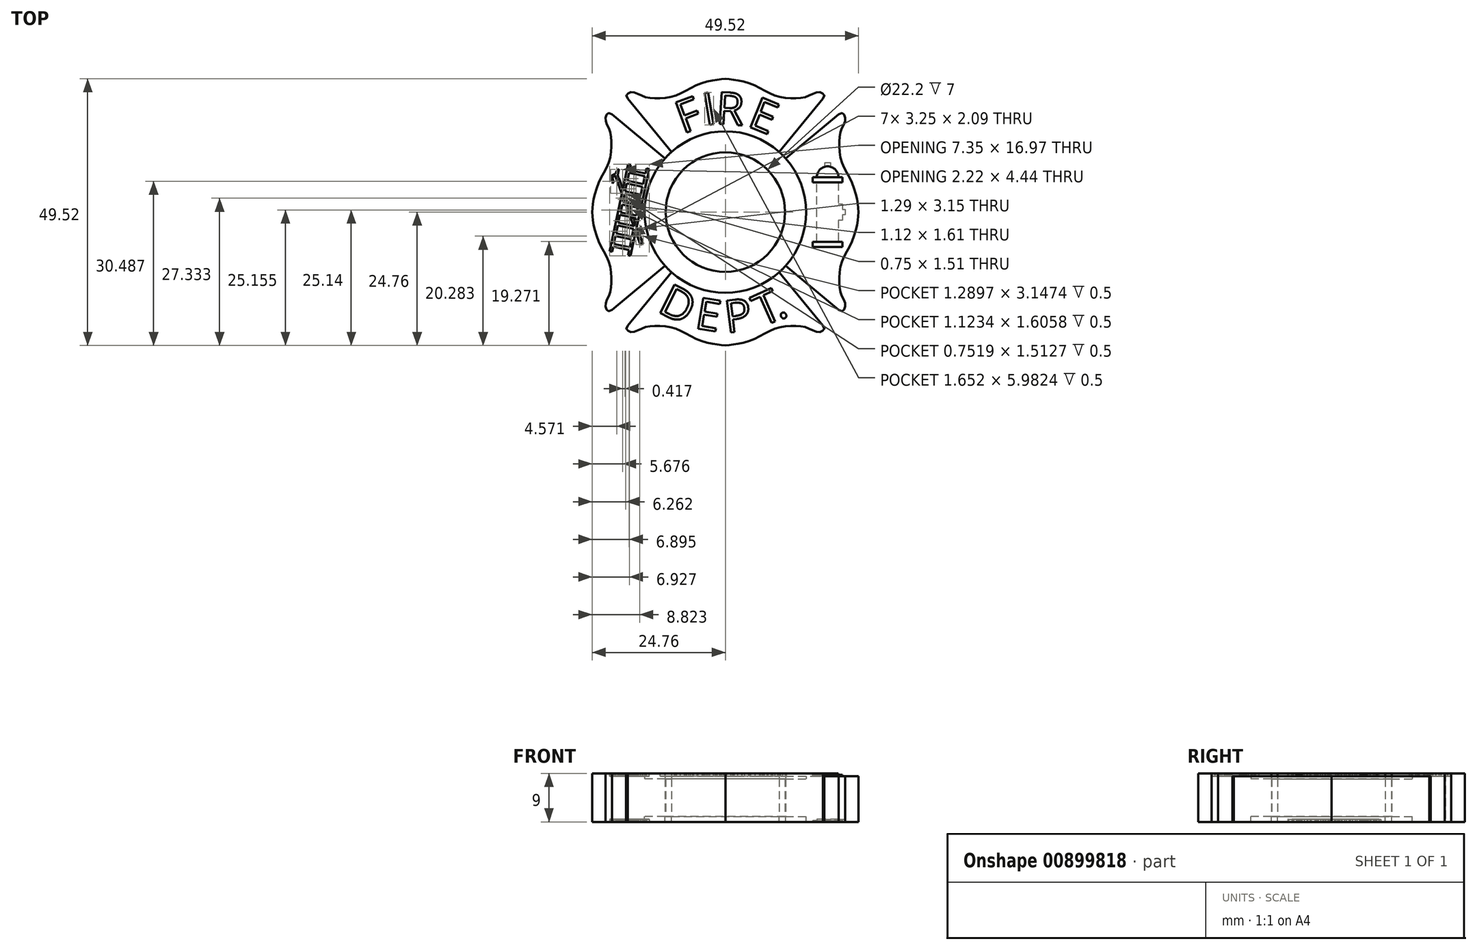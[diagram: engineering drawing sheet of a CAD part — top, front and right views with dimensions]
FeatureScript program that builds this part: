
annotation { "Feature Type Name" : "Feature", "Feature Type Description" : "" }
export const myFeature = defineFeature(function(context is Context, id is Id, definition is map)
    precondition{}
    {
        {
            var Q0;
            Q0=qCreatedBy(makeId("Top.planeOp"),FACE);
            var sketch = newSketch(context, id + "F0", { "sketchPlane" : qUnion([Q0])});
            skCircle(sketch, "E0", {"center": v(0, 0) * mm, "radius": 11.1 * mm});
            skCircle(sketch, "E1", {"center": v(0, 0) * mm, "radius": 15 * mm});
            skLineSegment(sketch, "E2", {"start": v(-30.5, 30.5) * mm, "end": v(0, 0) * mm, "construction": true});
            skLineSegment(sketch, "E3", {"start": v(0, 0) * mm, "end": v(35.07, -35.07) * mm, "construction": true});
            skLineSegment(sketch, "E4", {"start": v(31.52, 31.52) * mm, "end": v(-34.6, -34.6) * mm, "construction": true});
            skLineSegment(sketch, "E5", {"start": v(-10, 11.18) * mm, "end": v(-18.15, 21.05) * mm});
            skFitSpline(sketch, "E6", {"points": [v(-18.15, 21.05) * mm, v(-18.15, 22) * mm, v(-17.03, 22.25) * mm, v(-15.24, 21.5) * mm, v(-12.76, 21.15) * mm, v(-9.23, 21.64) * mm, v(-5.9, 23.34) * mm, v(-2.2, 24.5) * mm, v(0, 24.76) * mm], "startDerivative": vector(-16.22, 16.71) * mm, "endDerivative": vector(16.44, 1.31) * mm});
            skLineSegment(sketch, "E7", {"start": v(0, 15) * mm, "end": v(0, 24.76) * mm, "construction": true});
            skFitSpline(sketch, "E8.MirrorCS", {"points": [v(18.15, 21.05) * mm, v(18.15, 22) * mm, v(17.03, 22.25) * mm, v(15.24, 21.5) * mm, v(12.76, 21.15) * mm, v(9.23, 21.64) * mm, v(5.9, 23.34) * mm, v(2.2, 24.5) * mm, v(0, 24.76) * mm], "startDerivative": vector(16.22, 16.71) * mm, "endDerivative": vector(-16.44, 1.31) * mm});
            skLineSegment(sketch, "E9.MirrorCS", {"start": v(10, 11.18) * mm, "end": v(18.15, 21.05) * mm});
            skLineSegment(sketch, "E10", {"start": v(11.18, 10) * mm, "end": v(21.05, 18.15) * mm});
            skFitSpline(sketch, "E11", {"points": [v(21.05, 18.15) * mm, v(22, 18.15) * mm, v(22.25, 17.03) * mm, v(21.5, 15.24) * mm, v(21.15, 12.76) * mm, v(21.64, 9.23) * mm, v(23.34, 5.9) * mm, v(24.5, 2.2) * mm, v(24.76, 0) * mm], "startDerivative": vector(16.71, 16.22) * mm, "endDerivative": vector(1.31, -16.44) * mm});
            skLineSegment(sketch, "E12", {"start": v(15, 0) * mm, "end": v(24.76, 0) * mm, "construction": true});
            skFitSpline(sketch, "E13.MirrorCS", {"points": [v(21.05, -18.15) * mm, v(22, -18.15) * mm, v(22.25, -17.03) * mm, v(21.5, -15.24) * mm, v(21.15, -12.76) * mm, v(21.64, -9.23) * mm, v(23.34, -5.9) * mm, v(24.5, -2.2) * mm, v(24.76, 0) * mm], "startDerivative": vector(16.71, -16.22) * mm, "endDerivative": vector(1.31, 16.44) * mm});
            skLineSegment(sketch, "E14.MirrorCS", {"start": v(11.18, -10) * mm, "end": v(21.05, -18.15) * mm});
            skPoint(sketch, "E15", {"position": v(15, 0) * mm});
            skLineSegment(sketch, "E16", {"start": v(10, -11.18) * mm, "end": v(18.15, -21.05) * mm});
            skFitSpline(sketch, "E17", {"points": [v(18.15, -21.05) * mm, v(18.15, -22) * mm, v(17.03, -22.25) * mm, v(15.24, -21.5) * mm, v(12.76, -21.15) * mm, v(9.23, -21.64) * mm, v(5.9, -23.34) * mm, v(2.2, -24.5) * mm, v(0, -24.76) * mm], "startDerivative": vector(16.22, -16.71) * mm, "endDerivative": vector(-16.44, -1.31) * mm});
            skLineSegment(sketch, "E18", {"start": v(0, -15) * mm, "end": v(0, -24.76) * mm, "construction": true});
            skFitSpline(sketch, "E19.MirrorCS", {"points": [v(-18.15, -21.05) * mm, v(-18.15, -22) * mm, v(-17.03, -22.25) * mm, v(-15.24, -21.5) * mm, v(-12.76, -21.15) * mm, v(-9.23, -21.64) * mm, v(-5.9, -23.34) * mm, v(-2.2, -24.5) * mm, v(0, -24.76) * mm], "startDerivative": vector(-16.22, -16.71) * mm, "endDerivative": vector(16.44, -1.31) * mm});
            skLineSegment(sketch, "E20.MirrorCS", {"start": v(-10, -11.18) * mm, "end": v(-18.15, -21.05) * mm});
            skPoint(sketch, "E21", {"position": v(0, -15) * mm});
            skLineSegment(sketch, "E22", {"start": v(-11.18, -10) * mm, "end": v(-21.05, -18.15) * mm});
            skFitSpline(sketch, "E23", {"points": [v(-21.05, -18.15) * mm, v(-22, -18.15) * mm, v(-22.25, -17.03) * mm, v(-21.5, -15.24) * mm, v(-21.15, -12.76) * mm, v(-21.64, -9.23) * mm, v(-23.34, -5.9) * mm, v(-24.5, -2.2) * mm, v(-24.76, 0) * mm], "startDerivative": vector(-16.71, -16.22) * mm, "endDerivative": vector(-1.31, 16.44) * mm});
            skLineSegment(sketch, "E24", {"start": v(-15, 0) * mm, "end": v(-24.76, 0) * mm, "construction": true});
            skFitSpline(sketch, "E25.MirrorCS", {"points": [v(-21.05, 18.15) * mm, v(-22, 18.15) * mm, v(-22.25, 17.03) * mm, v(-21.5, 15.24) * mm, v(-21.15, 12.76) * mm, v(-21.64, 9.23) * mm, v(-23.34, 5.9) * mm, v(-24.5, 2.2) * mm, v(-24.76, 0) * mm], "startDerivative": vector(-16.71, 16.22) * mm, "endDerivative": vector(-1.31, -16.44) * mm});
            skLineSegment(sketch, "E26.MirrorCS", {"start": v(-11.18, 10) * mm, "end": v(-21.05, 18.15) * mm});
            skPoint(sketch, "E27", {"position": v(-15, 0) * mm});
            skSolve(sketch);
        }
        {
            var Q0;
            {var subQ0=sQuery(id+"F0.wireOp",EDGE,"E22");Q0=makeQuery(id+"F0.imprint","IMPRINT",FACE,{"disambiguationData":[TD([[makeQuery(id+"F0.imprint","IMPRINT",EDGE,{"derivedFrom":subQ0}),-1.0]])]});}
            var Q1;
            {var subQ0=sQuery(id+"F0.wireOp",EDGE,"E5");Q1=makeQuery(id+"F0.imprint","IMPRINT",FACE,{"disambiguationData":[TD([[makeQuery(id+"F0.imprint","IMPRINT",EDGE,{"derivedFrom":subQ0}),-1.0]])]});}
            var Q2;
            {var subQ0=sQuery(id+"F0.wireOp",EDGE,"E10");Q2=makeQuery(id+"F0.imprint","IMPRINT",FACE,{"disambiguationData":[TD([[makeQuery(id+"F0.imprint","IMPRINT",EDGE,{"derivedFrom":subQ0}),-1.0]])]});}
            var Q3;
            {var subQ0=sQuery(id+"F0.wireOp",EDGE,"E16");Q3=makeQuery(id+"F0.imprint","IMPRINT",FACE,{"disambiguationData":[TD([[makeQuery(id+"F0.imprint","IMPRINT",EDGE,{"derivedFrom":subQ0}),-1.0]])]});}
            var Q4;
            Q4=makeQuery(id+"F0.imprint","IMPRINT",FACE,{"disambiguationData":[TD([[makeQuery(id+"F0.imprint","IMPRINT",EDGE,{"derivedFrom":sQuery(id+"F0.wireOp",EDGE,"E0")}),-1.0]])]});
            extrude(context, id + "F1", {"entities" : qUnion([Q0, Q1, Q2, Q3, Q4]), "depth" : 7 * mm, "offsetDistance" : 25 * mm});
        }
        {
            var Q0;
            {var subQ0=sQuery(id+"F0.wireOp",EDGE,"E5");Q0=makeQuery(id+"F0.imprint","IMPRINT",FACE,{"disambiguationData":[TD([[makeQuery(id+"F0.imprint","IMPRINT",EDGE,{"derivedFrom":subQ0}),-1.0]])]});}
            var Q1;
            {var subQ0=sQuery(id+"F0.wireOp",EDGE,"E22");Q1=makeQuery(id+"F0.imprint","IMPRINT",FACE,{"disambiguationData":[TD([[makeQuery(id+"F0.imprint","IMPRINT",EDGE,{"derivedFrom":subQ0}),-1.0]])]});}
            var Q2;
            {var subQ0=sQuery(id+"F0.wireOp",EDGE,"E16");Q2=makeQuery(id+"F0.imprint","IMPRINT",FACE,{"disambiguationData":[TD([[makeQuery(id+"F0.imprint","IMPRINT",EDGE,{"derivedFrom":subQ0}),-1.0]])]});}
            var Q3;
            {var subQ0=sQuery(id+"F0.wireOp",EDGE,"E10");Q3=makeQuery(id+"F0.imprint","IMPRINT",FACE,{"disambiguationData":[TD([[makeQuery(id+"F0.imprint","IMPRINT",EDGE,{"derivedFrom":subQ0}),-1.0]])]});}
            extrude(context, id + "F2", {"entities" : qUnion([Q0, Q1, Q2, Q3]), "operationType" : NewBodyOperationType.ADD, "depth" : 8 * mm, "offsetDistance" : 25 * mm});
        }
        {
            var Q0;
            {var subQ0=sQuery(id+"F0.wireOp",EDGE,"E5");Q0=makeQuery(id+"F0.imprint","IMPRINT",FACE,{"disambiguationData":[TD([[makeQuery(id+"F0.imprint","IMPRINT",EDGE,{"derivedFrom":subQ0}),-1.0]])]});}
            var Q1;
            {var subQ0=sQuery(id+"F0.wireOp",EDGE,"E22");Q1=makeQuery(id+"F0.imprint","IMPRINT",FACE,{"disambiguationData":[TD([[makeQuery(id+"F0.imprint","IMPRINT",EDGE,{"derivedFrom":subQ0}),-1.0]])]});}
            var Q2;
            {var subQ0=sQuery(id+"F0.wireOp",EDGE,"E16");Q2=makeQuery(id+"F0.imprint","IMPRINT",FACE,{"disambiguationData":[TD([[makeQuery(id+"F0.imprint","IMPRINT",EDGE,{"derivedFrom":subQ0}),-1.0]])]});}
            var Q3;
            {var subQ0=sQuery(id+"F0.wireOp",EDGE,"E10");Q3=makeQuery(id+"F0.imprint","IMPRINT",FACE,{"disambiguationData":[TD([[makeQuery(id+"F0.imprint","IMPRINT",EDGE,{"derivedFrom":subQ0}),-1.0]])]});}
            extrude(context, id + "F3", {"entities" : qUnion([Q0, Q1, Q2, Q3]), "operationType" : NewBodyOperationType.ADD, "oppositeDirection" : true, "depth" : 1 * mm, "offsetDistance" : 25 * mm});
        }
        {
            var Q0;
            Q0=makeQuery(id+"F2.opExtrude","CAP_FACE",FACE,{"disambiguationData":[OSD([sQuery(id+"F0.wireOp",EDGE,"E1"),sQuery(id+"F0.wireOp",EDGE,"E22"),sQuery(id+"F0.wireOp",EDGE,"E23"),sQuery(id+"F0.wireOp",EDGE,"E25.MirrorCS"),sQuery(id+"F0.wireOp",EDGE,"E26.MirrorCS")])],"isStart":false});
            var sketch = newSketch(context, id + "F4", { "sketchPlane" : qUnion([Q0])});
            skLineSegment(sketch, "E28", {"start": v(-14.16, 8.03) * mm, "end": v(-17.6, -8.1) * mm});
            skLineSegment(sketch, "E29", {"start": v(-17.6, -8.1) * mm, "end": v(-18.09, -8) * mm});
            skLineSegment(sketch, "E30", {"start": v(-18.09, -8) * mm, "end": v(-14.65, 8.14) * mm});
            skLineSegment(sketch, "E31", {"start": v(-14.65, 8.14) * mm, "end": v(-14.16, 8.03) * mm});
            skLineSegment(sketch, "E32", {"start": v(-14.16, 8.03) * mm, "end": v(-18.88, 9.04) * mm, "construction": true});
            skLineSegment(sketch, "E33", {"start": v(-17.6, -8.1) * mm, "end": v(-22.13, -7.14) * mm, "construction": true});
            skLineSegment(sketch, "E34", {"start": v(-17.58, 8.76) * mm, "end": v(-21.02, -7.38) * mm});
            skLineSegment(sketch, "E35", {"start": v(-21.02, -7.38) * mm, "end": v(-21.5, -7.27) * mm});
            skLineSegment(sketch, "E36", {"start": v(-21.5, -7.27) * mm, "end": v(-18.07, 8.87) * mm});
            skLineSegment(sketch, "E37", {"start": v(-18.07, 8.87) * mm, "end": v(-17.58, 8.76) * mm});
            skLineSegment(sketch, "E38", {"start": v(-17.79, 7.78) * mm, "end": v(-14.85, 7.16) * mm});
            skLineSegment(sketch, "E39", {"start": v(-14.96, 6.67) * mm, "end": v(-17.9, 7.3) * mm});
            skLineSegment(sketch, "E40", {"start": v(-18.2, 5.83) * mm, "end": v(-15.27, 5.2) * mm});
            skLineSegment(sketch, "E41", {"start": v(-15.38, 4.71) * mm, "end": v(-18.3, 5.34) * mm});
            skLineSegment(sketch, "E42", {"start": v(-18.62, 3.87) * mm, "end": v(-15.69, 3.25) * mm});
            skLineSegment(sketch, "E43", {"start": v(-15.8, 2.76) * mm, "end": v(-18.73, 3.38) * mm});
            skLineSegment(sketch, "E44", {"start": v(-19.04, 1.91) * mm, "end": v(-16.1, 1.29) * mm});
            skLineSegment(sketch, "E45", {"start": v(-16.2, 0.8) * mm, "end": v(-19.14, 1.43) * mm});
            skLineSegment(sketch, "E46", {"start": v(-19.46, -0.04) * mm, "end": v(-16.52, -0.67) * mm});
            skLineSegment(sketch, "E47", {"start": v(-16.63, -1.16) * mm, "end": v(-19.56, -0.53) * mm});
            skLineSegment(sketch, "E48", {"start": v(-19.56, -0.53) * mm, "end": v(-19.87, -2) * mm});
            skLineSegment(sketch, "E49", {"start": v(-19.87, -2) * mm, "end": v(-16.94, -2.62) * mm});
            skLineSegment(sketch, "E50", {"start": v(-17.04, -3.11) * mm, "end": v(-19.98, -2.49) * mm});
            skLineSegment(sketch, "E51", {"start": v(-20.3, -3.95) * mm, "end": v(-17.36, -4.58) * mm});
            skLineSegment(sketch, "E52", {"start": v(-17.46, -5.07) * mm, "end": v(-20.4, -4.44) * mm});
            skLineSegment(sketch, "E53", {"start": v(-20.7, -5.9) * mm, "end": v(-17.77, -6.53) * mm});
            skLineSegment(sketch, "E54", {"start": v(-20.81, -6.4) * mm, "end": v(-17.88, -7.02) * mm});
            skLineSegment(sketch, "E55", {"start": v(-15.76, -6.05) * mm, "end": v(-20.25, 6.15) * mm, "construction": true});
            skLineSegment(sketch, "E56", {"start": v(-15.07, -6.49) * mm, "end": v(-19.96, 6.8) * mm, "construction": true});
            skLineSegment(sketch, "E57", {"start": v(-15.76, -6.05) * mm, "end": v(-16.58, -3.82) * mm});
            skLineSegment(sketch, "E58", {"start": v(-16.58, -3.82) * mm, "end": v(-16.39, -2.9) * mm});
            skLineSegment(sketch, "E59", {"start": v(-16.39, -2.9) * mm, "end": v(-15.3, -5.88) * mm});
            skLineSegment(sketch, "E60", {"start": v(-15.3, -5.88) * mm, "end": v(-15.76, -6.05) * mm});
            skLineSegment(sketch, "E61", {"start": v(-17.6, -1.07) * mm, "end": v(-17.02, -1.19) * mm});
            skLineSegment(sketch, "E62", {"start": v(-17.02, -1.19) * mm, "end": v(-16.84, -1.66) * mm});
            skLineSegment(sketch, "E63", {"start": v(-16.84, -1.66) * mm, "end": v(-17.02, -2.48) * mm});
            skLineSegment(sketch, "E64", {"start": v(-17.02, -2.48) * mm, "end": v(-17.08, -2.47) * mm});
            skLineSegment(sketch, "E65", {"start": v(-17.08, -2.47) * mm, "end": v(-17.6, -1.07) * mm});
            skLineSegment(sketch, "E66", {"start": v(-18.43, 1.2) * mm, "end": v(-17.85, 1.07) * mm});
            skLineSegment(sketch, "E67", {"start": v(-17.85, 1.07) * mm, "end": v(-17.3, -0.4) * mm});
            skLineSegment(sketch, "E68", {"start": v(-17.3, -0.4) * mm, "end": v(-17.88, -0.28) * mm});
            skLineSegment(sketch, "E69", {"start": v(-17.88, -0.28) * mm, "end": v(-18.43, 1.2) * mm});
            skLineSegment(sketch, "E70", {"start": v(-18.7, 1.92) * mm, "end": v(-18.87, 2.41) * mm});
            skLineSegment(sketch, "E71", {"start": v(-18.87, 2.41) * mm, "end": v(-18.68, 3.33) * mm});
            skLineSegment(sketch, "E72", {"start": v(-18.68, 3.33) * mm, "end": v(-18.12, 1.82) * mm});
            skLineSegment(sketch, "E73", {"start": v(-18.12, 1.82) * mm, "end": v(-18.7, 1.92) * mm});
            skLineSegment(sketch, "E74", {"start": v(-19.08, 4.42) * mm, "end": v(-19.28, 3.5) * mm});
            skLineSegment(sketch, "E75", {"start": v(-19.28, 3.5) * mm, "end": v(-20.25, 6.15) * mm});
            skLineSegment(sketch, "E76", {"start": v(-19.78, 6.32) * mm, "end": v(-19.08, 4.42) * mm});
            skFitSpline(sketch, "E77", {"points": [v(-19.78, 6.32) * mm, v(-19.96, 7.04) * mm, v(-19.78, 7.9) * mm, v(-19.84, 7.95) * mm, v(-20.28, 7.46) * mm, v(-20.46, 6.94) * mm, v(-20.25, 6.15) * mm], "startDerivative": vector(-1.58, 3.39) * mm, "endDerivative": vector(1.53, -4.27) * mm});
            skFitSpline(sketch, "E78", {"points": [v(-20.43, 7.13) * mm, v(-21.1, 6.77) * mm, v(-21.26, 6.52) * mm, v(-21.29, 6.26) * mm, v(-21.12, 5.99) * mm, v(-20.94, 5.63) * mm, v(-20.98, 5.3) * mm], "startDerivative": vector(-3.35, -1.51) * mm, "endDerivative": vector(-0.53, -2.06) * mm});
            skFitSpline(sketch, "E79", {"points": [v(-20.44, 6.78) * mm, v(-20.84, 6.57) * mm, v(-20.93, 6.46) * mm, v(-20.95, 6.32) * mm, v(-20.9, 6.1) * mm, v(-20.76, 5.66) * mm, v(-20.98, 5.3) * mm], "startDerivative": vector(-2.3, -1.02) * mm, "endDerivative": vector(-1.6, -1.65) * mm});
            skSolve(sketch);
        }
        {
            var Q0;
            Q0=makeQuery(id+"F4.imprint","IMPRINT",FACE,{"disambiguationData":[TD([[makeQuery(id+"F4.imprint","IMPRINT",EDGE,{"derivedFrom":sQuery(id+"F4.wireOp",EDGE,"E74")}),-1.0]])]});
            var Q1;
            {var subQ0=sQuery(id+"F4.wireOp",EDGE,"E78");Q1=makeQuery(id+"F4.imprint","IMPRINT",FACE,{"disambiguationData":[TD([[makeQuery(id+"F4.imprint","IMPRINT",EDGE,{"derivedFrom":subQ0}),1.0]])]});}
            var Q2;
            {var subQ17=sQuery(id+"F4.wireOp",EDGE,"E35");Q2=makeQuery(id+"F4.imprint","IMPRINT",FACE,{"disambiguationData":[TD([[makeQuery(id+"F4.imprint","IMPRINT",EDGE,{"derivedFrom":subQ17}),-1.0]])]});}
            var Q3;
            Q3=makeQuery(id+"F4.imprint","IMPRINT",FACE,{"disambiguationData":[TD([[makeQuery(id+"F4.imprint","IMPRINT",EDGE,{"derivedFrom":sQuery(id+"F4.wireOp",EDGE,"E28")}),-1.0]])]});
            var Q4;
            {var subQ0=sQuery(id+"F4.wireOp",EDGE,"E38");Q4=makeQuery(id+"F4.imprint","IMPRINT",FACE,{"disambiguationData":[TD([[makeQuery(id+"F4.imprint","IMPRINT",EDGE,{"derivedFrom":subQ0}),-1.0]])]});}
            var Q5;
            {var subQ0=sQuery(id+"F4.wireOp",EDGE,"E40");Q5=makeQuery(id+"F4.imprint","IMPRINT",FACE,{"disambiguationData":[TD([[makeQuery(id+"F4.imprint","IMPRINT",EDGE,{"derivedFrom":subQ0}),-1.0]])]});}
            var Q6;
            {var subQ0=sQuery(id+"F4.wireOp",EDGE,"E42");Q6=makeQuery(id+"F4.imprint","IMPRINT",FACE,{"disambiguationData":[TD([[makeQuery(id+"F4.imprint","IMPRINT",EDGE,{"derivedFrom":subQ0}),-1.0]])]});}
            var Q7;
            Q7=makeQuery(id+"F4.imprint","IMPRINT",FACE,{"disambiguationData":[TD([[makeQuery(id+"F4.imprint","IMPRINT",EDGE,{"derivedFrom":sQuery(id+"F4.wireOp",EDGE,"E70")}),-1.0]])]});
            var Q8;
            {var subQ0=sQuery(id+"F4.wireOp",EDGE,"E44");Q8=makeQuery(id+"F4.imprint","IMPRINT",FACE,{"disambiguationData":[TD([[makeQuery(id+"F4.imprint","IMPRINT",EDGE,{"derivedFrom":subQ0}),-1.0]])]});}
            var Q9;
            Q9=makeQuery(id+"F4.imprint","IMPRINT",FACE,{"disambiguationData":[TD([[makeQuery(id+"F4.imprint","IMPRINT",EDGE,{"derivedFrom":sQuery(id+"F4.wireOp",EDGE,"E66")}),-1.0]])]});
            var Q10;
            {var subQ0=sQuery(id+"F4.wireOp",EDGE,"E46");Q10=makeQuery(id+"F4.imprint","IMPRINT",FACE,{"disambiguationData":[TD([[makeQuery(id+"F4.imprint","IMPRINT",EDGE,{"derivedFrom":subQ0}),-1.0]])]});}
            var Q11;
            Q11=makeQuery(id+"F4.imprint","IMPRINT",FACE,{"disambiguationData":[TD([[makeQuery(id+"F4.imprint","IMPRINT",EDGE,{"derivedFrom":sQuery(id+"F4.wireOp",EDGE,"E61")}),-1.0]])]});
            var Q12;
            {var subQ0=sQuery(id+"F4.wireOp",EDGE,"E49");Q12=makeQuery(id+"F4.imprint","IMPRINT",FACE,{"disambiguationData":[TD([[makeQuery(id+"F4.imprint","IMPRINT",EDGE,{"derivedFrom":subQ0}),-1.0]])]});}
            var Q13;
            {var subQ0=sQuery(id+"F4.wireOp",EDGE,"E51");Q13=makeQuery(id+"F4.imprint","IMPRINT",FACE,{"disambiguationData":[TD([[makeQuery(id+"F4.imprint","IMPRINT",EDGE,{"derivedFrom":subQ0}),-1.0]])]});}
            var Q14;
            {var subQ0=sQuery(id+"F4.wireOp",EDGE,"E53");Q14=makeQuery(id+"F4.imprint","IMPRINT",FACE,{"disambiguationData":[TD([[makeQuery(id+"F4.imprint","IMPRINT",EDGE,{"derivedFrom":subQ0}),-1.0]])]});}
            var Q15;
            Q15=makeQuery(id+"F4.imprint","IMPRINT",FACE,{"disambiguationData":[TD([[makeQuery(id+"F4.imprint","IMPRINT",EDGE,{"derivedFrom":sQuery(id+"F4.wireOp",EDGE,"E57")}),-1.0]])]});
            extrude(context, id + "F5", {"entities" : qUnion([Q0, Q1, Q2, Q3, Q4, Q5, Q6, Q7, Q8, Q9, Q10, Q11, Q12, Q13, Q14, Q15]), "operationType" : NewBodyOperationType.ADD, "oppositeDirection" : true, "depth" : 9.5 * mm, "offsetDistance" : 25 * mm});
        }
        {
            var Q0;
            Q0=makeQuery(id+"F4.imprint","IMPRINT",FACE,{"disambiguationData":[TD([[makeQuery(id+"F4.imprint","IMPRINT",EDGE,{"derivedFrom":sQuery(id+"F4.wireOp",EDGE,"E74")}),-1.0]])]});
            var Q1;
            {var subQ0=sQuery(id+"F4.wireOp",EDGE,"E78");Q1=makeQuery(id+"F4.imprint","IMPRINT",FACE,{"disambiguationData":[TD([[makeQuery(id+"F4.imprint","IMPRINT",EDGE,{"derivedFrom":subQ0}),1.0]])]});}
            var Q2;
            {var subQ17=sQuery(id+"F4.wireOp",EDGE,"E35");Q2=makeQuery(id+"F4.imprint","IMPRINT",FACE,{"disambiguationData":[TD([[makeQuery(id+"F4.imprint","IMPRINT",EDGE,{"derivedFrom":subQ17}),-1.0]])]});}
            var Q3;
            {var subQ0=sQuery(id+"F4.wireOp",EDGE,"E38");Q3=makeQuery(id+"F4.imprint","IMPRINT",FACE,{"disambiguationData":[TD([[makeQuery(id+"F4.imprint","IMPRINT",EDGE,{"derivedFrom":subQ0}),-1.0]])]});}
            var Q4;
            Q4=makeQuery(id+"F4.imprint","IMPRINT",FACE,{"disambiguationData":[TD([[makeQuery(id+"F4.imprint","IMPRINT",EDGE,{"derivedFrom":sQuery(id+"F4.wireOp",EDGE,"E28")}),-1.0]])]});
            var Q5;
            {var subQ0=sQuery(id+"F4.wireOp",EDGE,"E40");Q5=makeQuery(id+"F4.imprint","IMPRINT",FACE,{"disambiguationData":[TD([[makeQuery(id+"F4.imprint","IMPRINT",EDGE,{"derivedFrom":subQ0}),-1.0]])]});}
            var Q6;
            {var subQ0=sQuery(id+"F4.wireOp",EDGE,"E42");Q6=makeQuery(id+"F4.imprint","IMPRINT",FACE,{"disambiguationData":[TD([[makeQuery(id+"F4.imprint","IMPRINT",EDGE,{"derivedFrom":subQ0}),-1.0]])]});}
            var Q7;
            Q7=makeQuery(id+"F4.imprint","IMPRINT",FACE,{"disambiguationData":[TD([[makeQuery(id+"F4.imprint","IMPRINT",EDGE,{"derivedFrom":sQuery(id+"F4.wireOp",EDGE,"E70")}),-1.0]])]});
            var Q8;
            {var subQ0=sQuery(id+"F4.wireOp",EDGE,"E44");Q8=makeQuery(id+"F4.imprint","IMPRINT",FACE,{"disambiguationData":[TD([[makeQuery(id+"F4.imprint","IMPRINT",EDGE,{"derivedFrom":subQ0}),-1.0]])]});}
            var Q9;
            Q9=makeQuery(id+"F4.imprint","IMPRINT",FACE,{"disambiguationData":[TD([[makeQuery(id+"F4.imprint","IMPRINT",EDGE,{"derivedFrom":sQuery(id+"F4.wireOp",EDGE,"E66")}),-1.0]])]});
            var Q10;
            {var subQ0=sQuery(id+"F4.wireOp",EDGE,"E46");Q10=makeQuery(id+"F4.imprint","IMPRINT",FACE,{"disambiguationData":[TD([[makeQuery(id+"F4.imprint","IMPRINT",EDGE,{"derivedFrom":subQ0}),-1.0]])]});}
            var Q11;
            Q11=makeQuery(id+"F4.imprint","IMPRINT",FACE,{"disambiguationData":[TD([[makeQuery(id+"F4.imprint","IMPRINT",EDGE,{"derivedFrom":sQuery(id+"F4.wireOp",EDGE,"E61")}),-1.0]])]});
            var Q12;
            {var subQ0=sQuery(id+"F4.wireOp",EDGE,"E49");Q12=makeQuery(id+"F4.imprint","IMPRINT",FACE,{"disambiguationData":[TD([[makeQuery(id+"F4.imprint","IMPRINT",EDGE,{"derivedFrom":subQ0}),-1.0]])]});}
            var Q13;
            {var subQ0=sQuery(id+"F4.wireOp",EDGE,"E51");Q13=makeQuery(id+"F4.imprint","IMPRINT",FACE,{"disambiguationData":[TD([[makeQuery(id+"F4.imprint","IMPRINT",EDGE,{"derivedFrom":subQ0}),-1.0]])]});}
            var Q14;
            {var subQ0=sQuery(id+"F4.wireOp",EDGE,"E53");Q14=makeQuery(id+"F4.imprint","IMPRINT",FACE,{"disambiguationData":[TD([[makeQuery(id+"F4.imprint","IMPRINT",EDGE,{"derivedFrom":subQ0}),-1.0]])]});}
            var Q15;
            Q15=makeQuery(id+"F4.imprint","IMPRINT",FACE,{"disambiguationData":[TD([[makeQuery(id+"F4.imprint","IMPRINT",EDGE,{"derivedFrom":sQuery(id+"F4.wireOp",EDGE,"E57")}),-1.0]])]});
            extrude(context, id + "F6", {"entities" : qUnion([Q0, Q1, Q2, Q3, Q4, Q5, Q6, Q7, Q8, Q9, Q10, Q11, Q12, Q13, Q14, Q15]), "operationType" : NewBodyOperationType.REMOVE, "oppositeDirection" : true, "depth" : .5 * mm, "offsetDistance" : 25 * mm});
        }
        {
            var Q0;
            Q0=makeQuery(id+"F5.opExtrude","CAP_FACE",FACE,{"disambiguationData":[OSD([sQuery(id+"F4.wireOp",EDGE,"E28"),sQuery(id+"F4.wireOp",EDGE,"E29"),sQuery(id+"F4.wireOp",EDGE,"E30"),sQuery(id+"F4.wireOp",EDGE,"E31"),sQuery(id+"F4.wireOp",EDGE,"E34"),sQuery(id+"F4.wireOp",EDGE,"E35"),sQuery(id+"F4.wireOp",EDGE,"E36"),sQuery(id+"F4.wireOp",EDGE,"E37"),sQuery(id+"F4.wireOp",EDGE,"E38"),sQuery(id+"F4.wireOp",EDGE,"E39"),sQuery(id+"F4.wireOp",EDGE,"E40"),sQuery(id+"F4.wireOp",EDGE,"E41"),sQuery(id+"F4.wireOp",EDGE,"E42"),sQuery(id+"F4.wireOp",EDGE,"E43"),sQuery(id+"F4.wireOp",EDGE,"E44"),sQuery(id+"F4.wireOp",EDGE,"E45"),sQuery(id+"F4.wireOp",EDGE,"E46"),sQuery(id+"F4.wireOp",EDGE,"E47"),sQuery(id+"F4.wireOp",EDGE,"E48"),sQuery(id+"F4.wireOp",EDGE,"E49"),sQuery(id+"F4.wireOp",EDGE,"E50"),sQuery(id+"F4.wireOp",EDGE,"E51"),sQuery(id+"F4.wireOp",EDGE,"E52"),sQuery(id+"F4.wireOp",EDGE,"E53"),sQuery(id+"F4.wireOp",EDGE,"E54")])],"isStart":false});
            var Q1;
            Q1=makeQuery(id+"F5.opExtrude","CAP_FACE",FACE,{"disambiguationData":[OSD([sQuery(id+"F4.wireOp",EDGE,"E74"),sQuery(id+"F4.wireOp",EDGE,"E75"),sQuery(id+"F4.wireOp",EDGE,"E76"),sQuery(id+"F4.wireOp",EDGE,"E77"),sQuery(id+"F4.wireOp",EDGE,"E78"),sQuery(id+"F4.wireOp",EDGE,"E79")])],"isStart":false});
            var Q2;
            Q2=makeQuery(id+"F5.opExtrude","CAP_FACE",FACE,{"disambiguationData":[OSD([sQuery(id+"F4.wireOp",EDGE,"E70"),sQuery(id+"F4.wireOp",EDGE,"E71"),sQuery(id+"F4.wireOp",EDGE,"E72"),sQuery(id+"F4.wireOp",EDGE,"E73")])],"isStart":false});
            var Q3;
            Q3=makeQuery(id+"F5.opExtrude","CAP_FACE",FACE,{"disambiguationData":[OSD([sQuery(id+"F4.wireOp",EDGE,"E66"),sQuery(id+"F4.wireOp",EDGE,"E67"),sQuery(id+"F4.wireOp",EDGE,"E68"),sQuery(id+"F4.wireOp",EDGE,"E69")])],"isStart":false});
            var Q4;
            Q4=makeQuery(id+"F5.opExtrude","CAP_FACE",FACE,{"disambiguationData":[OSD([sQuery(id+"F4.wireOp",EDGE,"E61"),sQuery(id+"F4.wireOp",EDGE,"E62"),sQuery(id+"F4.wireOp",EDGE,"E63"),sQuery(id+"F4.wireOp",EDGE,"E64"),sQuery(id+"F4.wireOp",EDGE,"E65")])],"isStart":false});
            var Q5;
            Q5=makeQuery(id+"F5.opExtrude","CAP_FACE",FACE,{"disambiguationData":[OSD([sQuery(id+"F4.wireOp",EDGE,"E57"),sQuery(id+"F4.wireOp",EDGE,"E58"),sQuery(id+"F4.wireOp",EDGE,"E59"),sQuery(id+"F4.wireOp",EDGE,"E60")])],"isStart":false});
            extrude(context, id + "F7", {"entities" : qUnion([Q0, Q1, Q2, Q3, Q4, Q5]), "operationType" : NewBodyOperationType.REMOVE, "oppositeDirection" : true, "depth" : 1 * mm, "offsetDistance" : 25 * mm});
        }
        {
            var Q0;
            Q0=makeQuery(id+"F2.opExtrude","CAP_FACE",FACE,{"disambiguationData":[OSD([sQuery(id+"F0.wireOp",EDGE,"E1"),sQuery(id+"F0.wireOp",EDGE,"E10"),sQuery(id+"F0.wireOp",EDGE,"E11"),sQuery(id+"F0.wireOp",EDGE,"E13.MirrorCS"),sQuery(id+"F0.wireOp",EDGE,"E14.MirrorCS")])],"isStart":false});
            var sketch = newSketch(context, id + "F8", { "sketchPlane" : qUnion([Q0])});
            skLineSegment(sketch, "E80", {"start": v(17, -5.5) * mm, "end": v(17, 5.5) * mm});
            skLineSegment(sketch, "E81", {"start": v(17, 5.5) * mm, "end": v(16.25, 5.5) * mm});
            skLineSegment(sketch, "E82", {"start": v(16.25, 5.5) * mm, "end": v(16.25, 6.5) * mm});
            skLineSegment(sketch, "E83", {"start": v(16.25, 6.5) * mm, "end": v(21.75, 6.5) * mm});
            skLineSegment(sketch, "E84", {"start": v(21.75, 6.5) * mm, "end": v(21.75, 5.5) * mm});
            skLineSegment(sketch, "E85", {"start": v(21.75, 5.5) * mm, "end": v(21, 5.5) * mm});
            skLineSegment(sketch, "E86", {"start": v(21, 5.5) * mm, "end": v(21, -5.5) * mm});
            skLineSegment(sketch, "E87", {"start": v(21, -5.5) * mm, "end": v(21.75, -5.5) * mm});
            skLineSegment(sketch, "E88", {"start": v(21.75, -5.5) * mm, "end": v(21.75, -6.5) * mm});
            skLineSegment(sketch, "E89", {"start": v(21.75, -6.5) * mm, "end": v(16.25, -6.5) * mm});
            skLineSegment(sketch, "E90", {"start": v(16.25, -6.5) * mm, "end": v(16.25, -5.5) * mm});
            skLineSegment(sketch, "E91", {"start": v(16.25, -5.5) * mm, "end": v(17, -5.5) * mm});
            skPoint(sketch, "E92", {"position": v(17, 0) * mm});
            skLineSegment(sketch, "E93", {"start": v(21, 1.5) * mm, "end": v(21.75, 1.5) * mm});
            skLineSegment(sketch, "E94", {"start": v(21.75, 1.5) * mm, "end": v(21.75, 0.5) * mm});
            skLineSegment(sketch, "E95", {"start": v(21.75, 0.5) * mm, "end": v(22.25, 0.5) * mm});
            skLineSegment(sketch, "E96", {"start": v(22.25, 0.5) * mm, "end": v(22.25, -0.5) * mm});
            skLineSegment(sketch, "E97", {"start": v(22.25, -0.5) * mm, "end": v(21.75, -0.5) * mm});
            skLineSegment(sketch, "E98", {"start": v(21.75, -0.5) * mm, "end": v(21.75, -1.5) * mm});
            skLineSegment(sketch, "E99", {"start": v(21.75, -1.5) * mm, "end": v(21, -1.5) * mm});
            skPoint(sketch, "E100", {"position": v(22.25, 0) * mm});
            skArc(sketch, "E101", {"start": v(21, 6.5) * mm, "mid": v(19, 8.49) * mm, "end": v(17, 6.5) * mm});
            skPoint(sketch, "E101.startSnap0", {"position": v(19, 6.5) * mm});
            skPoint(sketch, "E101.endSnap0", {"position": v(19, 6.5) * mm});
            skLineSegment(sketch, "E102", {"start": v(18.5, 8.43) * mm, "end": v(18.5, 9.18) * mm});
            skLineSegment(sketch, "E103", {"start": v(18.5, 9.18) * mm, "end": v(19.5, 9.18) * mm});
            skLineSegment(sketch, "E104", {"start": v(19.5, 9.18) * mm, "end": v(19.5, 8.43) * mm});
            skPoint(sketch, "E105", {"position": v(19, 9.18) * mm});
            skLineSegment(sketch, "E106", {"start": v(17, 5.5) * mm, "end": v(21, 5.5) * mm});
            skLineSegment(sketch, "E107", {"start": v(17, -5.5) * mm, "end": v(21, -5.5) * mm});
            skSolve(sketch);
        }
        {
            var Q0;
            Q0=qSketchRegion(id+"F8",true);
            extrude(context, id + "F9", {"entities" : qUnion([Q0]), "operationType" : NewBodyOperationType.ADD, "oppositeDirection" : true, "depth" : 9.5 * mm, "offsetDistance" : 25 * mm});
        }
        {
            var Q0;
            Q0=makeQuery(id+"F8.imprint","IMPRINT",FACE,{"disambiguationData":[TD([[makeQuery(id+"F8.imprint","IMPRINT",EDGE,{"derivedFrom":sQuery(id+"F8.wireOp",EDGE,"E81")}),-1.0]])]});
            var Q1;
            Q1=makeQuery(id+"F8.imprint","IMPRINT",FACE,{"disambiguationData":[TD([[makeQuery(id+"F8.imprint","IMPRINT",EDGE,{"derivedFrom":sQuery(id+"F8.wireOp",EDGE,"E87")}),-1.0]])]});
            extrude(context, id + "F10", {"entities" : qUnion([Q0, Q1]), "operationType" : NewBodyOperationType.REMOVE, "oppositeDirection" : true, "depth" : .25 * mm, "offsetDistance" : 25 * mm});
        }
        {
            var Q0;
            Q0=makeQuery(id+"F8.imprint","IMPRINT",FACE,{"disambiguationData":[TD([[makeQuery(id+"F8.imprint","IMPRINT",EDGE,{"derivedFrom":sQuery(id+"F8.wireOp",EDGE,"E80")}),-1.0]])]});
            var Q1;
            {var subQ0=sQuery(id+"F8.wireOp",EDGE,"E93");Q1=makeQuery(id+"F8.imprint","IMPRINT",FACE,{"disambiguationData":[TD([[makeQuery(id+"F8.imprint","IMPRINT",EDGE,{"derivedFrom":subQ0}),-1.0]])]});}
            var Q2;
            {var subQ0=sQuery(id+"F8.wireOp",EDGE,"E101");var subQ1=sQuery(id+"F8.wireOp",EDGE,"E83");var subQ2=makeQuery(id+"F8.imprint","INTERSECT",VERTEX,{"disambiguationData":[OD(0.0)],"derivedFrom":[subQ1,subQ0]});Q2=makeQuery(id+"F8.imprint","IMPRINT",FACE,{"disambiguationData":[TD([[makeQuery(id+"F8.imprint","IMPRINT",EDGE,{"disambiguationData":[TD([[subQ2,1.0]])],"derivedFrom":subQ1}),1.0]])]});}
            var Q3;
            {var subQ0=sQuery(id+"F8.wireOp",EDGE,"E102");Q3=makeQuery(id+"F8.imprint","IMPRINT",FACE,{"disambiguationData":[TD([[makeQuery(id+"F8.imprint","IMPRINT",EDGE,{"derivedFrom":subQ0}),-1.0]])]});}
            extrude(context, id + "F11", {"entities" : qUnion([Q0, Q1, Q2, Q3]), "operationType" : NewBodyOperationType.REMOVE, "oppositeDirection" : true, "depth" : .5 * mm, "offsetDistance" : 25 * mm});
        }
        {
            var Q0;
            Q0=makeQuery(id+"F9.opExtrude","CAP_FACE",FACE,{"disambiguationData":[OSD([sQuery(id+"F8.wireOp",EDGE,"E80"),sQuery(id+"F8.wireOp",EDGE,"E81"),sQuery(id+"F8.wireOp",EDGE,"E82"),sQuery(id+"F8.wireOp",EDGE,"E83"),sQuery(id+"F8.wireOp",EDGE,"E84"),sQuery(id+"F8.wireOp",EDGE,"E85"),sQuery(id+"F8.wireOp",EDGE,"E86"),sQuery(id+"F8.wireOp",EDGE,"E87"),sQuery(id+"F8.wireOp",EDGE,"E88"),sQuery(id+"F8.wireOp",EDGE,"E89"),sQuery(id+"F8.wireOp",EDGE,"E90"),sQuery(id+"F8.wireOp",EDGE,"E91"),sQuery(id+"F8.wireOp",EDGE,"E93"),sQuery(id+"F8.wireOp",EDGE,"E94"),sQuery(id+"F8.wireOp",EDGE,"E95"),sQuery(id+"F8.wireOp",EDGE,"E96"),sQuery(id+"F8.wireOp",EDGE,"E97"),sQuery(id+"F8.wireOp",EDGE,"E98"),sQuery(id+"F8.wireOp",EDGE,"E99"),sQuery(id+"F8.wireOp",EDGE,"E101"),sQuery(id+"F8.wireOp",EDGE,"E102"),sQuery(id+"F8.wireOp",EDGE,"E103"),sQuery(id+"F8.wireOp",EDGE,"E104")])],"isStart":false});
            var sketch = newSketch(context, id + "F12", { "sketchPlane" : qUnion([Q0])});
            skLineSegment(sketch, "E108", {"start": v(21, -6.5) * mm, "end": v(17, -6.5) * mm});
            skLineSegment(sketch, "E109", {"start": v(17, -5.5) * mm, "end": v(21, -5.5) * mm});
            skLineSegment(sketch, "E110", {"start": v(17, 5.5) * mm, "end": v(21, 5.5) * mm});
            skSolve(sketch);
        }
        {
            var Q0;
            Q0=makeQuery(id+"F12.imprint","IMPRINT",FACE,{"disambiguationData":[TD([[makeQuery(id+"F12.imprint","IMPRINT",EDGE,{"derivedFrom":sQuery(id+"F12.wireOp",EDGE,"E108")}),-1.0]])]});
            var Q1;
            Q1=makeQuery(id+"F12.imprint","IMPRINT",FACE,{"disambiguationData":[TD([[makeQuery(id+"F12.imprint","IMPRINT",EDGE,{"derivedFrom":sQuery(id+"F12.wireOp",EDGE,"E110")}),1.0]])]});
            extrude(context, id + "F13", {"entities" : qUnion([Q0, Q1]), "operationType" : NewBodyOperationType.REMOVE, "oppositeDirection" : true, "depth" : .75 * mm, "offsetDistance" : 25 * mm});
        }
        {
            var Q0;
            {var subQ0=sQuery(id+"F8.wireOp",EDGE,"E103");var subQ1=sQuery(id+"F8.wireOp",EDGE,"E102");var subQ2=sQuery(id+"F8.wireOp",EDGE,"E101");var subQ3=sQuery(id+"F8.wireOp",EDGE,"E83");var subQ4=sQuery(id+"F8.wireOp",EDGE,"E104");Q0=makeQuery(id+"F13.boolean.opBoolean","SPLIT",FACE,{"disambiguationData":[TD([makeQuery(id+"F9.opExtrude","SWEPT_FACE",FACE,{"disambiguationData":[OSD([subQ1])]})])],"derivedFrom":makeQuery(id+"F9.opExtrude","CAP_FACE",FACE,{"disambiguationData":[OSD([sQuery(id+"F8.wireOp",EDGE,"E80"),sQuery(id+"F8.wireOp",EDGE,"E81"),sQuery(id+"F8.wireOp",EDGE,"E82"),subQ3,sQuery(id+"F8.wireOp",EDGE,"E84"),sQuery(id+"F8.wireOp",EDGE,"E85"),sQuery(id+"F8.wireOp",EDGE,"E86"),sQuery(id+"F8.wireOp",EDGE,"E87"),sQuery(id+"F8.wireOp",EDGE,"E88"),sQuery(id+"F8.wireOp",EDGE,"E89"),sQuery(id+"F8.wireOp",EDGE,"E90"),sQuery(id+"F8.wireOp",EDGE,"E91"),sQuery(id+"F8.wireOp",EDGE,"E93"),sQuery(id+"F8.wireOp",EDGE,"E94"),sQuery(id+"F8.wireOp",EDGE,"E95"),sQuery(id+"F8.wireOp",EDGE,"E96"),sQuery(id+"F8.wireOp",EDGE,"E97"),sQuery(id+"F8.wireOp",EDGE,"E98"),sQuery(id+"F8.wireOp",EDGE,"E99"),subQ2,subQ1,subQ0,subQ4])],"isStart":false})});}
            var Q1;
            {var subQ0=sQuery(id+"F8.wireOp",EDGE,"E96");var subQ1=sQuery(id+"F8.wireOp",EDGE,"E95");var subQ2=sQuery(id+"F8.wireOp",EDGE,"E94");var subQ3=sQuery(id+"F8.wireOp",EDGE,"E99");var subQ4=sQuery(id+"F8.wireOp",EDGE,"E80");var subQ5=sQuery(id+"F8.wireOp",EDGE,"E98");var subQ6=sQuery(id+"F8.wireOp",EDGE,"E87");var subQ7=sQuery(id+"F8.wireOp",EDGE,"E86");var subQ8=sQuery(id+"F8.wireOp",EDGE,"E97");var subQ9=sQuery(id+"F8.wireOp",EDGE,"E85");var subQ10=sQuery(id+"F8.wireOp",EDGE,"E93");var subQ11=sQuery(id+"F8.wireOp",EDGE,"E91");var subQ12=sQuery(id+"F8.wireOp",EDGE,"E81");Q1=makeQuery(id+"F13.boolean.opBoolean","SPLIT",FACE,{"disambiguationData":[TD([makeQuery(id+"F9.opExtrude","SWEPT_FACE",FACE,{"disambiguationData":[OSD([subQ4])]})])],"derivedFrom":makeQuery(id+"F9.opExtrude","CAP_FACE",FACE,{"disambiguationData":[OSD([subQ4,subQ12,sQuery(id+"F8.wireOp",EDGE,"E82"),sQuery(id+"F8.wireOp",EDGE,"E83"),sQuery(id+"F8.wireOp",EDGE,"E84"),subQ9,subQ7,subQ6,sQuery(id+"F8.wireOp",EDGE,"E88"),sQuery(id+"F8.wireOp",EDGE,"E89"),sQuery(id+"F8.wireOp",EDGE,"E90"),subQ11,subQ10,subQ2,subQ1,subQ0,subQ8,subQ5,subQ3,sQuery(id+"F8.wireOp",EDGE,"E101"),sQuery(id+"F8.wireOp",EDGE,"E102"),sQuery(id+"F8.wireOp",EDGE,"E103"),sQuery(id+"F8.wireOp",EDGE,"E104")])],"isStart":false})});}
            extrude(context, id + "F14", {"entities" : qUnion([Q0, Q1]), "operationType" : NewBodyOperationType.REMOVE, "oppositeDirection" : true, "depth" : 1 * mm, "offsetDistance" : 25 * mm});
        }
        {
            var Q0;
            Q0=makeQuery(id+"F2.opExtrude","CAP_FACE",FACE,{"disambiguationData":[OSD([sQuery(id+"F0.wireOp",EDGE,"E1"),sQuery(id+"F0.wireOp",EDGE,"E5"),sQuery(id+"F0.wireOp",EDGE,"E6"),sQuery(id+"F0.wireOp",EDGE,"E8.MirrorCS"),sQuery(id+"F0.wireOp",EDGE,"E9.MirrorCS")])],"isStart":false});
            var sketch = newSketch(context, id + "F15", { "sketchPlane" : qUnion([Q0])});
            skText(sketch, "E111", { "text": "F", "fontName": "OpenSans-Regular.ttf"});
            skCircle(sketch, "E112", {"center": v(0, 0) * mm, "radius": 16.5 * mm, "construction": true});
            skText(sketch, "E113", { "text": "I", "fontName": "OpenSans-Regular.ttf"});
            skText(sketch, "E114", { "text": "R", "fontName": "OpenSans-Regular.ttf"});
            skText(sketch, "E115", { "text": "E", "fontName": "OpenSans-Regular.ttf"});
            const initialGuessF15  = {"E111": [-0.00788, 0.0145, 0.93749, 0.34802, 0.006], "E113": [-0.0037, 0.01608, 0.98662, 0.16303, 0.006], "E114": [-0.00184, 0.0164, 0.99835, -0.05743, 0.006], "E115": [0.00391, 0.01603, 0.9281, -0.37235, 0.006]};
            skSetInitialGuess(sketch, initialGuessF15);
            skSolve(sketch);
        }
        {
            var Q0;
            Q0=makeQuery(id+"F15.imprint","IMPRINT",FACE,{"disambiguationData":[TD([[makeQuery(id+"F15.imprint","IMPRINT",EDGE,{"derivedFrom":sQuery(id+"F15.wireOp",EDGE,"E111.sketch_text.stroke-0")}),-1.0]])]});
            var Q1;
            Q1=makeQuery(id+"F15.imprint","IMPRINT",FACE,{"disambiguationData":[TD([[makeQuery(id+"F15.imprint","IMPRINT",EDGE,{"derivedFrom":sQuery(id+"F15.wireOp",EDGE,"E113.sketch_text.stroke-0")}),-1.0]])]});
            var Q2;
            Q2=makeQuery(id+"F15.imprint","IMPRINT",FACE,{"disambiguationData":[TD([[makeQuery(id+"F15.imprint","IMPRINT",EDGE,{"derivedFrom":sQuery(id+"F15.wireOp",EDGE,"E114.sketch_text.stroke-0")}),-1.0]])]});
            var Q3;
            Q3=makeQuery(id+"F15.imprint","IMPRINT",FACE,{"disambiguationData":[TD([[makeQuery(id+"F15.imprint","IMPRINT",EDGE,{"derivedFrom":sQuery(id+"F15.wireOp",EDGE,"E115.sketch_text.stroke-0")}),-1.0]])]});
            extrude(context, id + "F16", {"entities" : qUnion([Q0, Q1, Q2, Q3]), "operationType" : NewBodyOperationType.REMOVE, "oppositeDirection" : true, "depth" : .5 * mm, "offsetDistance" : 25 * mm});
        }
        {
            var Q0;
            Q0=makeQuery(id+"F2.opExtrude","CAP_FACE",FACE,{"disambiguationData":[OSD([sQuery(id+"F0.wireOp",EDGE,"E1"),sQuery(id+"F0.wireOp",EDGE,"E16"),sQuery(id+"F0.wireOp",EDGE,"E17"),sQuery(id+"F0.wireOp",EDGE,"E19.MirrorCS"),sQuery(id+"F0.wireOp",EDGE,"E20.MirrorCS")])],"isStart":false});
            var sketch = newSketch(context, id + "F17", { "sketchPlane" : qUnion([Q0])});
            skText(sketch, "E116", { "text": "D", "fontName": "OpenSans-Regular.ttf"});
            skText(sketch, "E117", { "text": "E", "fontName": "OpenSans-Regular.ttf"});
            skText(sketch, "E118", { "text": "P", "fontName": "OpenSans-Regular.ttf"});
            skText(sketch, "E119", { "text": "T", "fontName": "OpenSans-Regular.ttf"});
            skText(sketch, "E120", { "text": ".", "fontName": "OpenSans-Regular.ttf"});
            const initialGuessF17  = {"E116": [-0.01284, -0.01838, 0.89013, -0.4557, 0.006], "E117": [-0.00585, -0.02153, 0.98678, -0.16206, 0.00585], "E118": [0.00021, -0.02245, 0.99232, 0.12366, 0.006], "E119": [0.00682, -0.02139, 0.91234, 0.40943, 0.006], "E120": [0.01006, -0.02012, 0.87211, 0.4893, 0.006]};
            skSetInitialGuess(sketch, initialGuessF17);
            skSolve(sketch);
        }
        {
            var Q0;
            Q0=qSketchRegion(id+"F17",true);
            extrude(context, id + "F18", {"entities" : qUnion([Q0]), "operationType" : NewBodyOperationType.REMOVE, "oppositeDirection" : true, "depth" : .5 * mm, "offsetDistance" : 25 * mm});
        }
    });
